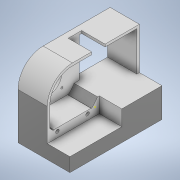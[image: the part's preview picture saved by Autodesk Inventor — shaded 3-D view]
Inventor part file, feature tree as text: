
AUTODESK INVENTOR PART (.ipt)
format: ipt  version: 2022 (Build 260153000, 153)  size: 1,333,248 bytes
history: mixed  units: mm
features: sketch x27, extrude x26, other x3, fillet x1, plane x1, imported_body x1
ambient origin geometry x8: Origin, YZ Plane, XZ Plane, XY Plane, X Axis, Y Axis, Z Axis, Center Point
bodies: Solid1 (imported_parasolid)
feature tree (59):
  other  "Assembly2.iam"
  other  "96Gears_Stage_1_modified.ipt:1"
  other  "96Gears_Stage_2_modified.ipt:1"
  extrude  "Extrusion3"  Depth=3.0mm
  extrude  "Extrusion5"  Depth=18.0mm TaperAngle=0.0deg
  extrude  "Extrusion6"  Depth=6.0mm TaperAngle=0.0deg
  extrude  "Extrusion7"  Depth=10.0mm TaperAngle=0.0deg
  extrude  "Extrusion8"  Depth=4.1mm
  extrude  "Extrusion9"  Depth=7.0mm
  extrude  "Extrusion10"  Depth=50.0mm TaperAngle=0.0deg
  extrude  "Extrusion11"  Depth=50.0mm TaperAngle=0.0deg
  extrude  "Extrusion12"  Depth=3.0mm TaperAngle=0.0deg
  extrude  "Extrusion13"  Depth=3.0mm TaperAngle=0.0deg
  extrude  "Extrusion14"  Depth=3.0mm TaperAngle=0.0deg
  extrude  "Extrusion15"  Depth=9.0mm TaperAngle=0.0deg
  extrude  "Extrusion16"  Depth=30.0mm
  fillet  "Fillet1"  Radius=5.0mm
  extrude  "Extrusion17"  Depth=10.0mm TaperAngle=0.0deg
  extrude  "Extrusion18"  Depth=10.0mm TaperAngle=0.0deg
  extrude  "Extrusion19"  Depth=1.25mm
  extrude  "Extrusion20"  Depth=10.0mm TaperAngle=0.0deg
  extrude  "Extrusion21"  Depth=10.0mm TaperAngle=0.0deg
  extrude  "Extrusion22"  Depth=10.0mm TaperAngle=0.0deg
  plane  "Work Plane1"
  extrude  "Extrusion26"  Depth=10.0mm TaperAngle=0.0deg
  extrude  "Extrusion27"  Depth=10.0mm
  extrude  "Extrusion28"  Depth=10.0mm TaperAngle=0.0deg
  extrude  "Extrusion29"  Depth=10.0mm TaperAngle=0.0deg
  extrude  "Extrusion30"  [1 undecoded]
  extrude  "Extrusion31"  [1 undecoded]
  extrude  "Extrusion32"  [1 undecoded]
  sketch  "Sketch5"  dims[d7=6.0mm d8=18.0mm d9=0.0mm]
  sketch  "Sketch4"  dims[d0=10.0mm d6=3.0mm]
  sketch  "Sketch7"  dims[d17=32.25mm d18=6.0mm d19=0.0mm]
  sketch  "Sketch8"  dims[d20=10.0mm d21=10.0mm d22=0.0mm]
  sketch  "Sketch9"  dims[d24=4.1mm d25=4.1mm]
  sketch  "Sketch10"  dims[d26=10.0mm d27=0.0mm d28=7.0mm]
  sketch  "Sketch11"  dims[d29=0.0mm d30=0.0mm d31=50.0mm d32=0.0mm]
  sketch  "Sketch12"  dims[d33=3.0mm d34=50.0mm d35=0.0mm]
  sketch  "Sketch13"  dims[d38=3.0mm d39=3.0mm d40=0.0mm]
  sketch  "Sketch14"  dims[d41=23.0mm d42=3.0mm d43=0.0mm]
  sketch  "Sketch15"  dims[d44=3.0mm d45=0.0mm d46=9.0mm d47=0.0mm]
  sketch  "Sketch16"  dims[d49=33.25mm d50=9.0mm d51=0.0mm]
  sketch  "Sketch17"  dims[d52=2.0mm d53=0.0mm d54=30.0mm d55=5.0mm]
  sketch  "Sketch18"  dims[d57=5.0mm d58=10.0mm d59=0.0mm]
  sketch  "Sketch19"  dims[d60=3.0mm d61=10.0mm d62=0.0mm]
  sketch  "Sketch20"  dims[d63=2.0mm d64=0.0mm d65=1.25mm]
  sketch  "Sketch21"  dims[d66=2.0mm d67=0.0mm d68=10.0mm d69=0.0mm]
  sketch  "Sketch22"  dims[d74=2.5mm d75=10.0mm d76=0.0mm]
  sketch  "Sketch23"  dims[d98=10.0mm d99=0.0mm d100=10.0mm d101=0.0mm]
  sketch  "Sketch25"  dims[d102=10.0mm d103=0.0mm d104=10.0mm d105=0.0mm]
  sketch  "Sketch29"  dims[d106=10.0mm d107=0.0mm d108=8.0mm]
  sketch  "Sketch30"  dims[d109=16.0mm d110=10.0mm d111=0.0mm]
  sketch  "Sketch31"  dims[d112=2.5mm d114=10.0mm d115=0.0mm]
  sketch  "Sketch32"
  sketch  "Sketch33"
  sketch  "Sketch34"
  sketch  "Sketch35"
  imported_body  NMx_Import_Brep_tag  [imported B-rep: ~36 faces, bbox_mm=[62.0, 85.0, 110.0]]
note: 3 required parameter values undecoded (feature->parameter linkage not recoverable at this tier; creation-order binding heuristic only, values carry confidence <= 0.55)
